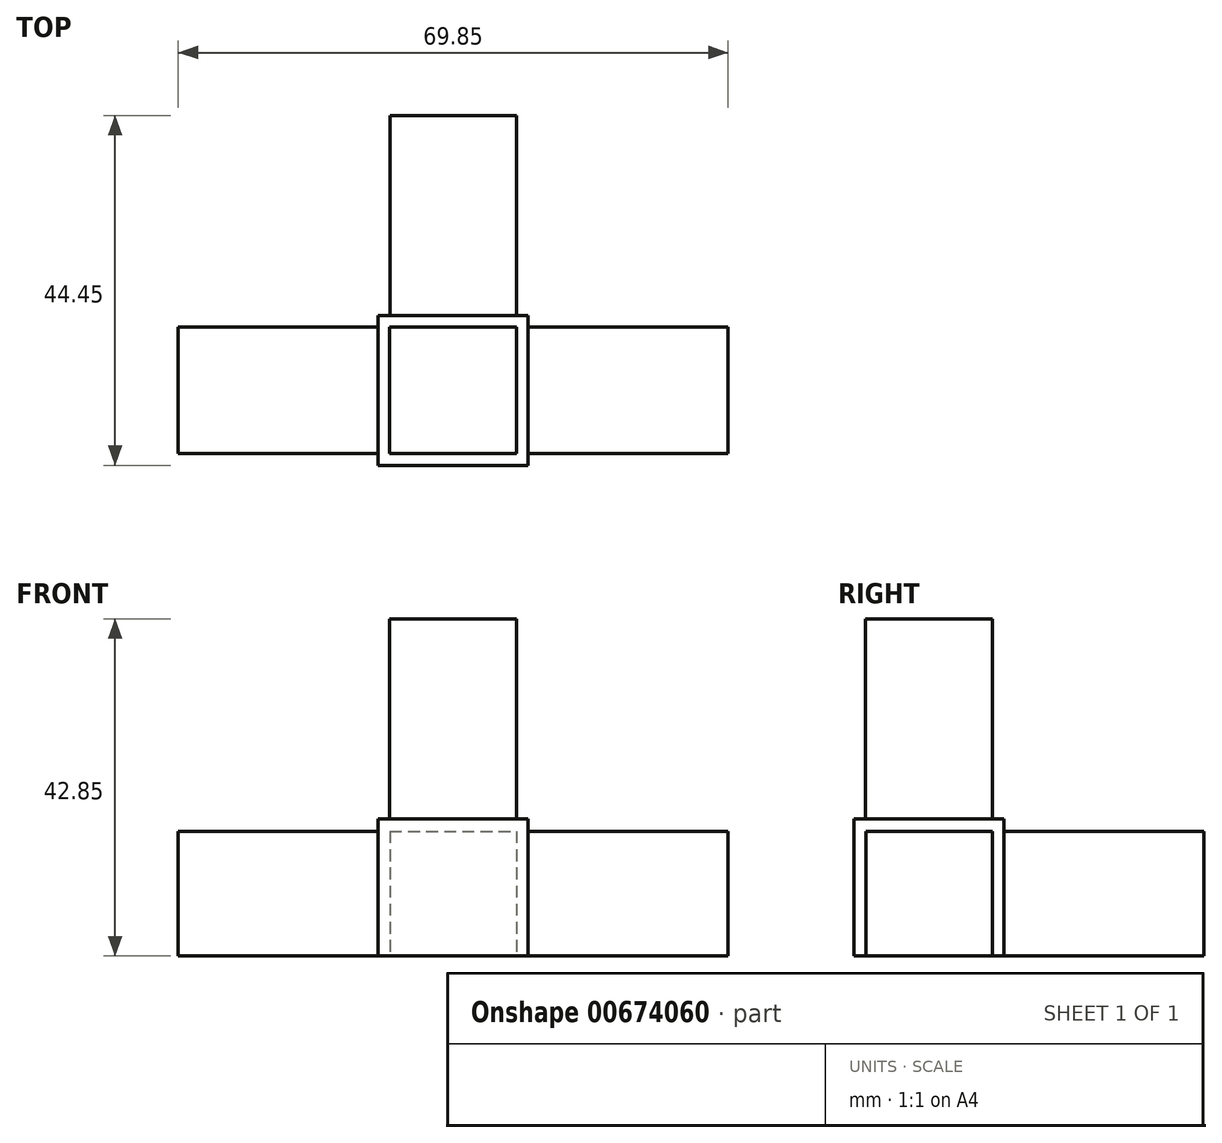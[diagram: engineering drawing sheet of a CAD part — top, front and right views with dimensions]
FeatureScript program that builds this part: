
annotation { "Feature Type Name" : "Feature", "Feature Type Description" : "" }
export const myFeature = defineFeature(function(context is Context, id is Id, definition is map)
    precondition{}
    {
        {
            var Q0;
            Q0=qCreatedBy(makeId("Top.planeOp"),FACE);
            var sketch = newSketch(context, id + "F0", { "sketchPlane" : qUnion([Q0])});
            skLineSegment(sketch, "E0", {"start": v(0, 1.5) * mm, "end": v(-25.4, 1.5) * mm});
            skLineSegment(sketch, "E1", {"start": v(-25.4, 1.5) * mm, "end": v(-25.4, 0) * mm});
            skLineSegment(sketch, "E2", {"start": v(-25.4, 0) * mm, "end": v(-44.45, 0) * mm});
            skLineSegment(sketch, "E3", {"start": v(-44.45, 0) * mm, "end": v(-44.45, 1.5) * mm});
            skLineSegment(sketch, "E4", {"start": v(-44.45, 1.5) * mm, "end": v(-69.85, 1.5) * mm});
            skLineSegment(sketch, "E5", {"start": v(-69.85, 1.5) * mm, "end": v(-69.85, 17.55) * mm});
            skLineSegment(sketch, "E6", {"start": v(-69.85, 17.55) * mm, "end": v(-44.45, 17.55) * mm});
            skLineSegment(sketch, "E7", {"start": v(-44.45, 17.55) * mm, "end": v(-44.45, 19.05) * mm});
            skLineSegment(sketch, "E8", {"start": v(-44.45, 19.05) * mm, "end": v(-42.95, 19.05) * mm});
            skLineSegment(sketch, "E9", {"start": v(-42.95, 19.05) * mm, "end": v(-42.95, 44.45) * mm});
            skLineSegment(sketch, "E10", {"start": v(-42.95, 44.45) * mm, "end": v(-26.9, 44.45) * mm});
            skLineSegment(sketch, "E11", {"start": v(-26.9, 44.45) * mm, "end": v(-26.9, 19.05) * mm});
            skLineSegment(sketch, "E12", {"start": v(-26.9, 19.05) * mm, "end": v(-25.4, 19.05) * mm});
            skLineSegment(sketch, "E13", {"start": v(-25.4, 19.05) * mm, "end": v(-25.4, 17.55) * mm});
            skLineSegment(sketch, "E14", {"start": v(-25.4, 17.55) * mm, "end": v(0, 17.55) * mm});
            skLineSegment(sketch, "E15", {"start": v(0, 17.55) * mm, "end": v(0, 1.5) * mm});
            skSolve(sketch);
        }
        {
            var Q0;
            Q0=makeQuery(id+"F0.imprint","IMPRINT",FACE,{"disambiguationData":[TD([[makeQuery(id+"F0.imprint","IMPRINT",EDGE,{"derivedFrom":sQuery(id+"F0.wireOp",EDGE,"E0")}),-1.0]])]});
            extrude(context, id + "F1", {"entities" : qUnion([Q0]), "depth" : 15.85 * mm, "offsetDistance" : 25 * mm});
        }
        {
            var Q0;
            Q0=makeQuery(id+"F1.opExtrude","CAP_FACE",FACE,{"disambiguationData":[OSD([sQuery(id+"F0.wireOp",EDGE,"E0"),sQuery(id+"F0.wireOp",EDGE,"E1"),sQuery(id+"F0.wireOp",EDGE,"E2"),sQuery(id+"F0.wireOp",EDGE,"E3"),sQuery(id+"F0.wireOp",EDGE,"E4"),sQuery(id+"F0.wireOp",EDGE,"E5"),sQuery(id+"F0.wireOp",EDGE,"E6"),sQuery(id+"F0.wireOp",EDGE,"E7"),sQuery(id+"F0.wireOp",EDGE,"E8"),sQuery(id+"F0.wireOp",EDGE,"E9"),sQuery(id+"F0.wireOp",EDGE,"E10"),sQuery(id+"F0.wireOp",EDGE,"E11"),sQuery(id+"F0.wireOp",EDGE,"E12"),sQuery(id+"F0.wireOp",EDGE,"E13"),sQuery(id+"F0.wireOp",EDGE,"E14"),sQuery(id+"F0.wireOp",EDGE,"E15")])],"isStart":false});
            var sketch = newSketch(context, id + "F2", { "sketchPlane" : qUnion([Q0])});
            skLineSegment(sketch, "E16.bottom", {"start": v(-44.45, 19.05) * mm, "end": v(-25.4, 19.05) * mm});
            skLineSegment(sketch, "E16.top", {"start": v(-44.45, 0) * mm, "end": v(-25.4, 0) * mm});
            skLineSegment(sketch, "E16.left", {"start": v(-44.45, 19.05) * mm, "end": v(-44.45, 0) * mm});
            skLineSegment(sketch, "E16.right", {"start": v(-25.4, 19.05) * mm, "end": v(-25.4, 0) * mm});
            skSolve(sketch);
        }
        {
            var Q0;
            {var subQ0=sQuery(id+"F2.wireOp",EDGE,"E16.top");Q0=makeQuery(id+"F2.imprint","IMPRINT",FACE,{"disambiguationData":[TD([[makeQuery(id+"F2.imprint","IMPRINT",EDGE,{"derivedFrom":subQ0}),-1.0]])]});}
            extrude(context, id + "F3", {"entities" : qUnion([Q0]), "operationType" : NewBodyOperationType.ADD, "depth" : 1.6 * mm, "offsetDistance" : 25 * mm});
        }
        {
            var Q0;
            Q0=makeQuery(id+"F3.opExtrude","CAP_FACE",FACE,{"disambiguationData":[OSD([sQuery(id+"F2.wireOp",EDGE,"E16.bottom"),sQuery(id+"F2.wireOp",EDGE,"E16.top"),sQuery(id+"F2.wireOp",EDGE,"E16.left"),sQuery(id+"F2.wireOp",EDGE,"E16.right")])],"isStart":false});
            var sketch = newSketch(context, id + "F4", { "sketchPlane" : qUnion([Q0])});
            skLineSegment(sketch, "E17.bottom", {"start": v(-26.88, 17.58) * mm, "end": v(-42.98, 17.58) * mm});
            skLineSegment(sketch, "E17.top", {"start": v(-26.88, 1.48) * mm, "end": v(-42.98, 1.48) * mm});
            skLineSegment(sketch, "E17.left", {"start": v(-26.88, 17.58) * mm, "end": v(-26.88, 1.48) * mm});
            skLineSegment(sketch, "E17.right", {"start": v(-42.98, 17.58) * mm, "end": v(-42.98, 1.48) * mm});
            skPoint(sketch, "E17.middle", {"position": v(-34.93, 9.53) * mm});
            skPoint(sketch, "E17.middle.positionSnap0", {"position": v(-25.4, 9.53) * mm});
            skPoint(sketch, "E17.middle.positionSnap1", {"position": v(-34.93, 19.05) * mm});
            skPoint(sketch, "E17.centerSnap0", {"position": v(-25.4, 9.53) * mm});
            skPoint(sketch, "E17.centerSnap1", {"position": v(-34.93, 19.05) * mm});
            skSolve(sketch);
        }
        {
            var Q0;
            Q0=makeQuery(id+"F4.imprint","IMPRINT",FACE,{"disambiguationData":[TD([[makeQuery(id+"F4.imprint","IMPRINT",EDGE,{"derivedFrom":sQuery(id+"F4.wireOp",EDGE,"E17.bottom")}),1.0]])]});
            extrude(context, id + "F5", {"entities" : qUnion([Q0]), "operationType" : NewBodyOperationType.ADD, "depth" : 25.4 * mm, "offsetDistance" : 25 * mm});
        }
    });
